FCSTD DOCUMENT  (FreeCAD 0.18.1R)
Label: Z_drive
License: All rights reserved
LicenseURL: http://en.wikipedia.org/wiki/All_rights_reserved
objects: Part::Feature×3, App::FeaturePython×2, App::Part×1, Part::Compound×1
note: 4 computed .brp shape members not serialized (recipe doc carries the construction recipe); baked Part::Feature solids carry a one-line shape summary decoded from their .brp

FEATURE [Part::Feature] Part__Feature  label="z_drive_rear_support_a_x2(Solid)"
  Placement = pos=(0,39.4,0) rot=(0.57735,0.57735,-0.57735;2.0944rad)
  shape: bbox 98.17 x 20 x 61.02 mm, 21513 faces (baked)
FEATURE [Part::Feature] Part__Feature001  label="Nema 17  Stepper Motor length 34mm"
  Placement = pos=(71,0,-118) rot=(0,-1,0;1.5708rad)
  shape: bbox 61.3 x 57.6 x 42.3 mm, 990 faces, 27 solids (baked)
FEATURE [Part::Feature] Part__Feature002  label="z_drive_front_support_a_x2(Solid)"
  Placement = pos=(-47.1424,-14.6346,-222.173) rot=(0.57735,0.57735,0.57735;4.18879rad)
  shape: bbox 42.14 x 14 x 55.19 mm, 30967 faces (baked)
FEATURE [App::Part] Part
  Group = -> [Part__Feature001,Part__Feature,Part__Feature002]
  Origin = -> Origin
FEATURE [Part::Compound] Compound
  Links = -> [Part__Feature001,Part__Feature,Part__Feature002]
FEATURE [App::FeaturePython] planeConstraint01  # a2plus constraint (typed FeaturePython)
  Object1 = Part__Feature
  Object2 = Part__Feature002
  SubElement1 = Face20513
  SubElement2 = Face30769
  Type = plane
  directionConstraint = 0
  offset = 0
FEATURE [App::FeaturePython] planeConstraint02  # a2plus constraint (typed FeaturePython)
  Object1 = Part__Feature
  Object2 = Part__Feature002
  SubElement1 = Face20317
  SubElement2 = Face30509
  Type = plane
  directionConstraint = 0
  offset = 0
